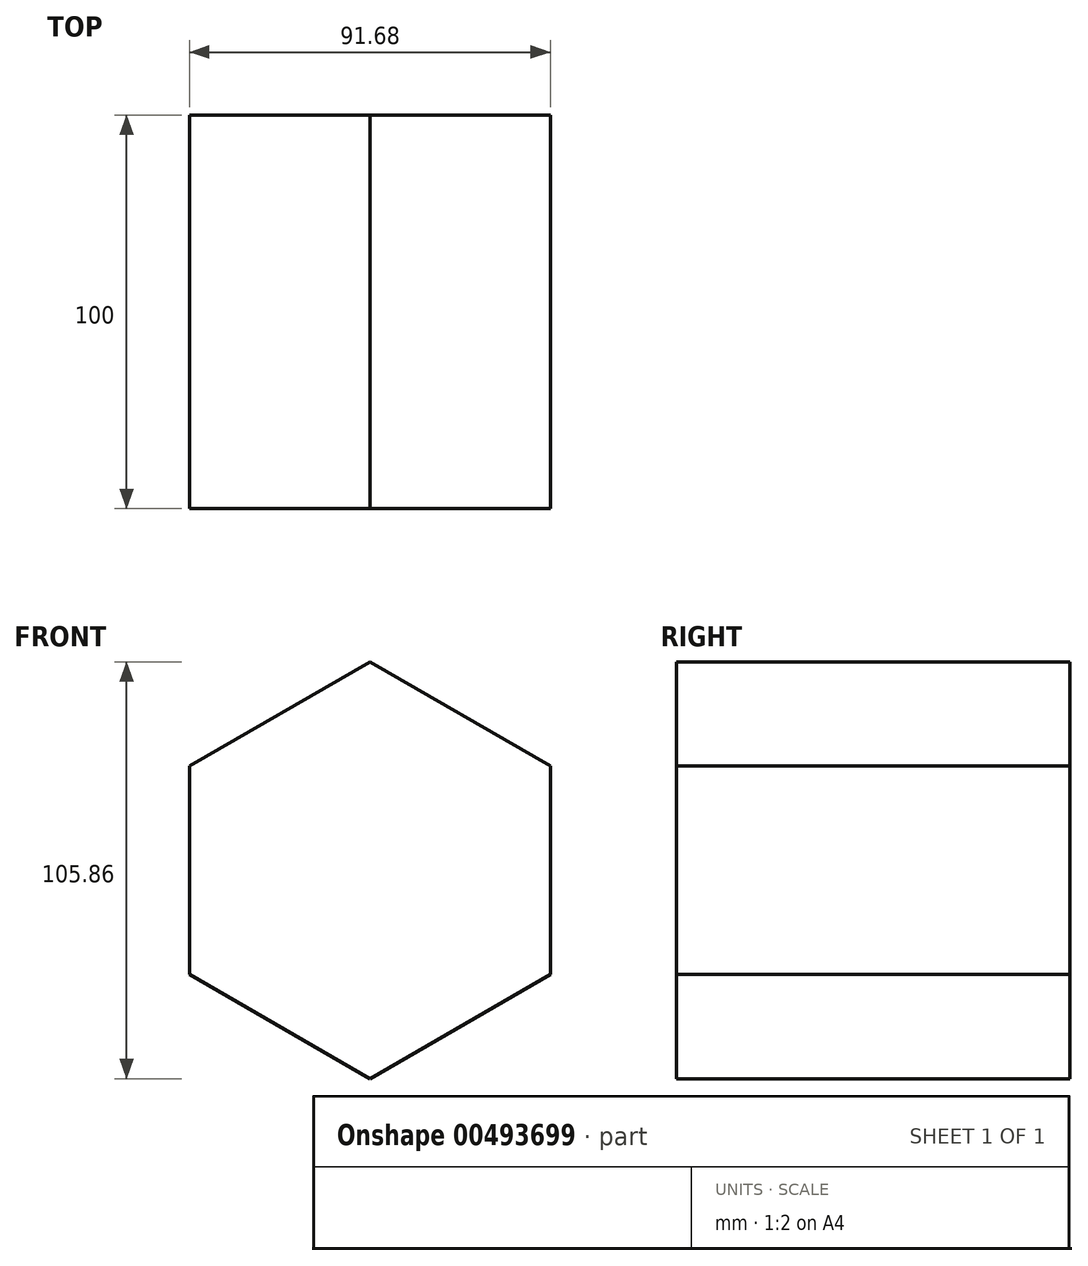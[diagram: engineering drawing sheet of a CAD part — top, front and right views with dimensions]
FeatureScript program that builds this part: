
annotation { "Feature Type Name" : "Feature", "Feature Type Description" : "" }
export const myFeature = defineFeature(function(context is Context, id is Id, definition is map)
    precondition{}
    {
        {
            var Q0;
            Q0=qCreatedBy(makeId("Front.planeOp"),FACE);
            var sketch = newSketch(context, id + "F0", { "sketchPlane" : qUnion([Q0])});
            skCircle(sketch, "E0.cCircle", {"center": v(0, 0) * mm, "radius": 52.93 * mm, "construction": true});
            skLineSegment(sketch, "E0.0", {"start": v(0, 52.93) * mm, "end": v(45.84, 26.47) * mm});
            skLineSegment(sketch, "E0.1", {"start": v(45.84, 26.47) * mm, "end": v(45.84, -26.47) * mm});
            skLineSegment(sketch, "E0.2", {"start": v(45.84, -26.47) * mm, "end": v(0, -52.93) * mm});
            skLineSegment(sketch, "E0.3", {"start": v(0, -52.93) * mm, "end": v(-45.84, -26.47) * mm});
            skLineSegment(sketch, "E0.4", {"start": v(-45.84, -26.47) * mm, "end": v(-45.84, 26.47) * mm});
            skLineSegment(sketch, "E0.5", {"start": v(-45.84, 26.47) * mm, "end": v(0, 52.93) * mm});
            skSolve(sketch);
        }
        {
            var Q0;
            Q0=makeQuery(id+"F0.imprint","IMPRINT",FACE,{"disambiguationData":[TD([[makeQuery(id+"F0.imprint","IMPRINT",EDGE,{"derivedFrom":sQuery(id+"F0.wireOp",EDGE,"E0.0")}),-1.0]])]});
            extrude(context, id + "F1", {"entities" : qUnion([Q0]), "depth" : 100 * mm});
        }
    });
